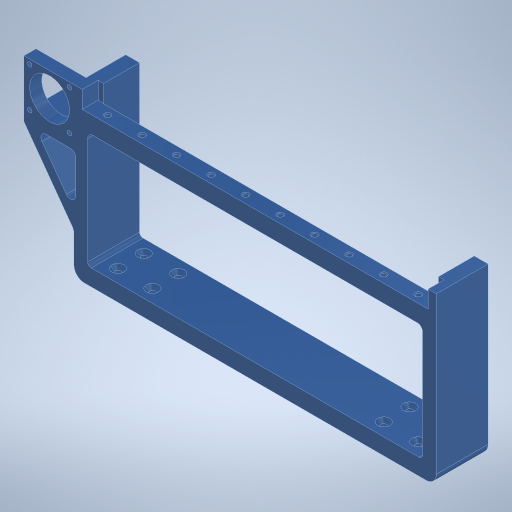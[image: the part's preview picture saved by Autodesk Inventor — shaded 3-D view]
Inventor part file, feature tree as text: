
AUTODESK INVENTOR PART (.ipt)
format: ipt  version: 2024.1 (Build 281209000, 209)  size: 448,512 bytes
history: native  units: in
note: dims shown in document units (in); Inventor stores cm internally (conversion verified against a paired STEP export)
features: extrude x12, sketch x12, fillet x5, chamfer x2
ambient origin geometry x8: Origin, YZ Plane, XZ Plane, XY Plane, X Axis, Y Axis, Z Axis, Center Point
bodies: Solid1 (feature_tree)
feature tree (31):
  extrude  "Extrusion1"  Depth=1.1811in
  extrude  "Extrusion2"  Depth=0.315in
  extrude  "Extrusion3"  Depth=1.1811in
  chamfer  "Chamfer1"  Distance=3.4252in
  fillet  "Fillet1"  Radius=0.122in
  fillet  "Fillet2"  Radius=0.122in
  extrude  "Extrusion4"  Depth=0.122in
  extrude  "Extrusion5"  Depth=0.122in
  extrude  "Extrusion6"  Depth=0.122in
  chamfer  "Chamfer2"  Distance=0.3937in
  extrude  "Extrusion7"  Depth=0.3937in
  extrude  "Extrusion8"  Depth=0.4528in
  extrude  "Extrusion9"  Depth=0.4528in
  fillet  "Fillet4"  Radius=0.3937in
  extrude  "Extrusion10"  Depth=0.3937in
  extrude  "Extrusion11"  Depth=0.4528in
  fillet  "Fillet5"  Radius=0.7874in
  fillet  "Fillet6"  Radius=0.5906in
  extrude  "Extrusion12"  Depth=0.7874in
  sketch  "Sketch1"  dims[d0=8.2677in d1=1.1811in]
  sketch  "Sketch2"  dims[d2=0.374in d3=0.0in d4=0.315in]
  sketch  "Sketch3"  dims[d5=0.315in d6=1.1811in d7=3.4252in d8=0.0in d9=0.122in d10=0.122in]
  sketch  "Sketch4"  dims[d11=0.122in d12=0.122in]
  sketch  "Sketch5"  dims[d13=0.122in d14=0.122in]
  sketch  "Sketch6"  dims[d15=0.122in d16=0.122in]
  sketch  "Sketch7"  dims[d17=0.7874in]
  sketch  "Sketch8"  dims[d18=0.5906in]
  sketch  "Sketch9"  dims[d19=0.7874in]
  sketch  "Sketch10"  dims[d20=0.5906in]
  sketch  "Sketch11"  dims[d21=0.2953in]
  sketch  "Sketch12"  dims[d22=0.2953in d23=0.3937in d24=0.3937in d25=0.2953in d26=0.2953in d27=0.3937in d28=0.3937in d29=0.5906in d30=0.7874in d31=0.5906in d32=0.7874in d33=0.0in d34=0.0in d35=0.0787in d36=0.0787in d37=45.0deg d38=0.0787in d39=0.2362in d40=0.3937in d41=0.3937in d42=0.3543in d43=0.0in d44=0.126in d45=0.3622in d46=0.126in d47=0.3622in d48=0.3543in d49=0.0in d50=0.1024in d51=0.1772in d52=0.4016in d53=3.937in d55=0.7874in d56=0.3937in d58=0.3937in d60=0.3937in d61=0.0in d62=0.0197in d63=0.0787in d64=45.0deg d65=0.2756in d66=1.2992in d67=1.1417in d68=0.0in d69=0.189in d70=1.1417in d71=0.0in d72=0.9055in d73=0.5551in d74=0.5551in d75=0.0in d76=0.0in d78=0.1181in d79=1.5748in d80=0.3937in d81=0.0in d82=0.189in d83=0.2756in d85=0.9055in d86=0.0in d87=0.0in d88=0.1181in d89=0.2362in d90=0.1024in d91=0.1024in d92=0.1024in d93=0.1024in d94=0.4528in d95=0.4528in d96=0.4528in d97=0.4528in d98=0.4528in d99=0.4528in d100=0.4528in d101=0.4528in d102=0.0in d103=0.0in]
